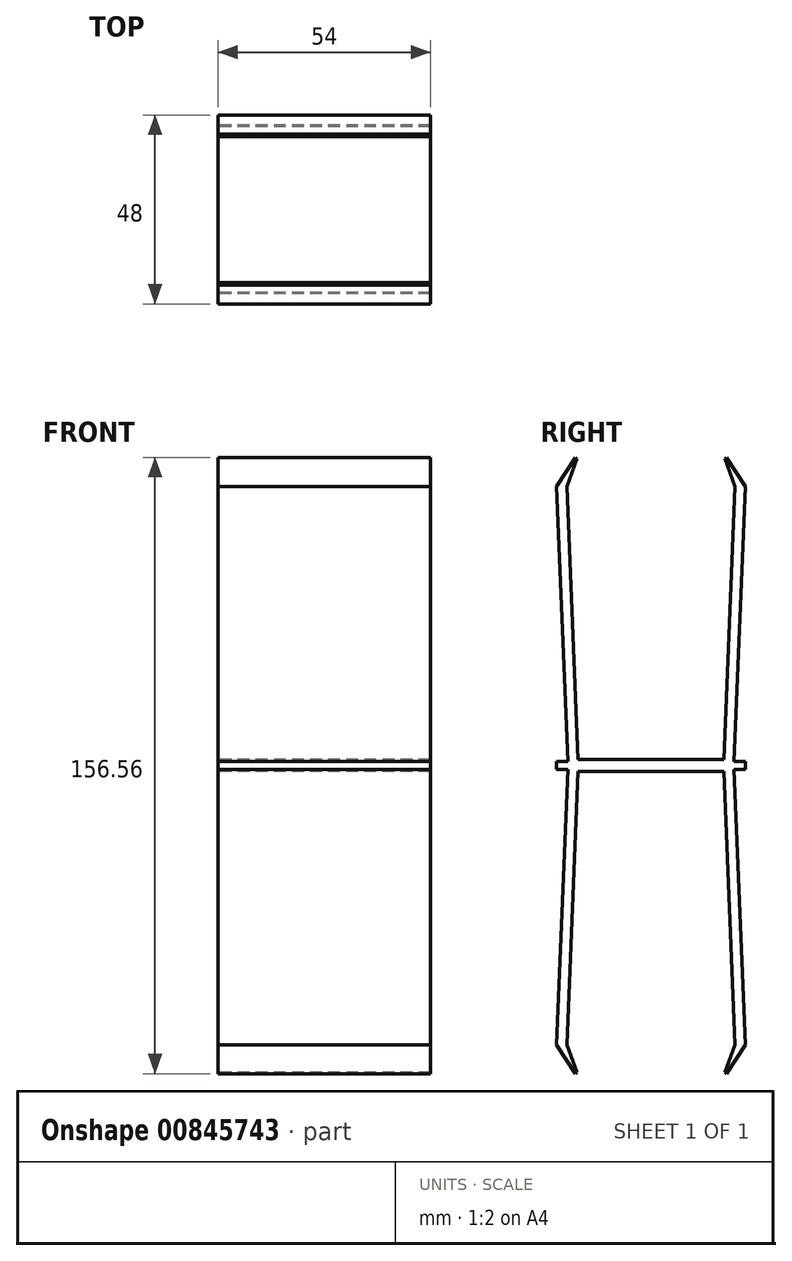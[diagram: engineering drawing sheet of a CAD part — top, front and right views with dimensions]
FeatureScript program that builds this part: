
annotation { "Feature Type Name" : "Feature", "Feature Type Description" : "" }
export const myFeature = defineFeature(function(context is Context, id is Id, definition is map)
    precondition{}
    {
        {
            var Q0;
            Q0=qCreatedBy(makeId("Right.planeOp"),FACE);
            var sketch = newSketch(context, id + "F0", { "sketchPlane" : qUnion([Q0])});
            skLineSegment(sketch, "E0", {"start": v(0, 0) * mm, "end": v(-24, 0) * mm});
            skLineSegment(sketch, "E1", {"start": v(-24, 0) * mm, "end": v(-24, 1) * mm});
            skLineSegment(sketch, "E2", {"start": v(-24, 1) * mm, "end": v(-21.1, 1) * mm});
            skLineSegment(sketch, "E3", {"start": v(-21.1, 1) * mm, "end": v(-24, 70.94) * mm});
            skLineSegment(sketch, "E4", {"start": v(-24, 70.94) * mm, "end": v(-19.16, 78.28) * mm});
            skLineSegment(sketch, "E5", {"start": v(-19.16, 78.28) * mm, "end": v(-18.74, 78) * mm});
            skLineSegment(sketch, "E6", {"start": v(-18.74, 78) * mm, "end": v(-21.4, 70.94) * mm});
            skLineSegment(sketch, "E7", {"start": v(-21.4, 70.94) * mm, "end": v(-18.52, 1.5) * mm});
            skLineSegment(sketch, "E8", {"start": v(-18.52, 1.5) * mm, "end": v(0, 1.5) * mm});
            skLineSegment(sketch, "E9", {"start": v(0, 1.5) * mm, "end": v(0, 0) * mm});
            skLineSegment(sketch, "E10", {"start": v(-24, 1) * mm, "end": v(-24, 88.7) * mm, "construction": true});
            skLineSegment(sketch, "E11", {"start": v(-24, 70.94) * mm, "end": v(-17.67, 70.94) * mm, "construction": true});
            skSolve(sketch);
        }
        {
            var Q0;
            Q0 = qSketchRegion(id + "F0", true);
            extrude(context, id + "F1", {"entities" : qUnion([Q0]), "depth" : 54 * mm, "offsetDistance" : 25 * mm});
        }
        {
            var Q0;
            Q0=makeQuery(id+"F1.opExtrude","SWEPT_BODY",BODY,{"disambiguationData":[OSD([sQuery(id+"F0.wireOp",EDGE,"E0"),sQuery(id+"F0.wireOp",EDGE,"E1"),sQuery(id+"F0.wireOp",EDGE,"E2"),sQuery(id+"F0.wireOp",EDGE,"E3"),sQuery(id+"F0.wireOp",EDGE,"E4"),sQuery(id+"F0.wireOp",EDGE,"E5"),sQuery(id+"F0.wireOp",EDGE,"E6"),sQuery(id+"F0.wireOp",EDGE,"E7"),sQuery(id+"F0.wireOp",EDGE,"E8"),sQuery(id+"F0.wireOp",EDGE,"E9")])]});
            var Q1;
            Q1=qCreatedBy(makeId("Front.planeOp"),FACE);
            mirror(context, id + "F2", {"operationType" : NewBodyOperationType.ADD, "entities" : qUnion([Q0]), "mirrorPlane" : qUnion([Q1])});
        }
        {
            var Q0;
            Q0=makeQuery(id+"F1.opExtrude","SWEPT_BODY",BODY,{"disambiguationData":[OSD([sQuery(id+"F0.wireOp",EDGE,"E0"),sQuery(id+"F0.wireOp",EDGE,"E1"),sQuery(id+"F0.wireOp",EDGE,"E2"),sQuery(id+"F0.wireOp",EDGE,"E3"),sQuery(id+"F0.wireOp",EDGE,"E4"),sQuery(id+"F0.wireOp",EDGE,"E5"),sQuery(id+"F0.wireOp",EDGE,"E6"),sQuery(id+"F0.wireOp",EDGE,"E7"),sQuery(id+"F0.wireOp",EDGE,"E8"),sQuery(id+"F0.wireOp",EDGE,"E9")])]});
            var Q1;
            Q1=qCreatedBy(makeId("Top.planeOp"),FACE);
            mirror(context, id + "F3", {"operationType" : NewBodyOperationType.ADD, "entities" : qUnion([Q0]), "mirrorPlane" : qUnion([Q1])});
        }
    });
